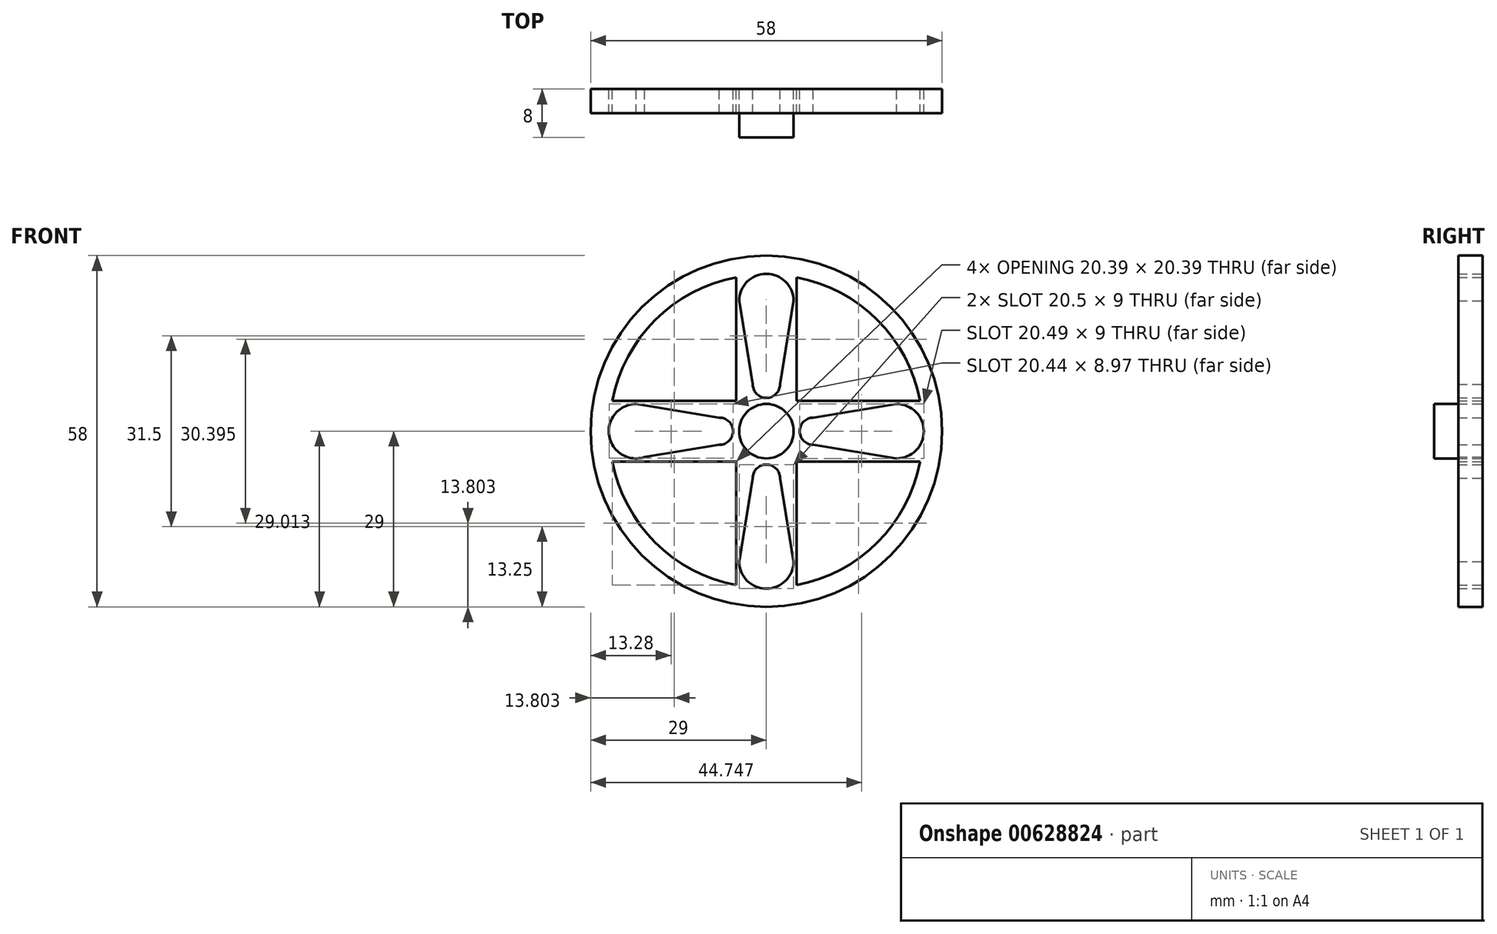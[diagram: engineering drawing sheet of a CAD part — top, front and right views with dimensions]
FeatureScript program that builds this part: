
annotation { "Feature Type Name" : "Feature", "Feature Type Description" : "" }
export const myFeature = defineFeature(function(context is Context, id is Id, definition is map)
    precondition{}
    {
        {
            var Q0;
            Q0=qCreatedBy(makeId("Front.planeOp"),FACE);
            var sketch = newSketch(context, id + "F0", { "sketchPlane" : qUnion([Q0])});
            skCircle(sketch, "E0", {"center": v(0, 0) * mm, "radius": 27 * mm});
            skCircle(sketch, "E1", {"center": v(0, 0) * mm, "radius": 4.5 * mm});
            skCircle(sketch, "E2", {"center": v(0, 0) * mm, "radius": 29 * mm});
            skArc(sketch, "E3", {"start": v(-21.5, 4.5) * mm, "mid": v(-25.94, -0.73) * mm, "end": v(-20.07, -4.27) * mm});
            skArc(sketch, "E4", {"start": v(4.5, 21.5) * mm, "mid": v(0, 26) * mm, "end": v(-4.5, 21.5) * mm});
            skArc(sketch, "E5", {"start": v(-4.5, -21.5) * mm, "mid": v(0, -26) * mm, "end": v(4.5, -21.5) * mm});
            skArc(sketch, "E6", {"start": v(-7.75, -2.25) * mm, "mid": v(-5.5, 0) * mm, "end": v(-7.75, 2.25) * mm});
            skArc(sketch, "E7", {"start": v(2.25, -7.75) * mm, "mid": v(0, -5.5) * mm, "end": v(-2.25, -7.75) * mm});
            skArc(sketch, "E8", {"start": v(7.75, 2.25) * mm, "mid": v(5.5, 0) * mm, "end": v(7.75, -2.25) * mm});
            skArc(sketch, "E9", {"start": v(-2.25, 7.75) * mm, "mid": v(0, 5.5) * mm, "end": v(2.25, 7.75) * mm});
            skLineSegment(sketch, "E10", {"start": v(-21.5, 4.5) * mm, "end": v(-7.75, 2.25) * mm});
            skLineSegment(sketch, "E11", {"start": v(-20.07, -4.27) * mm, "end": v(-7.75, -2.25) * mm});
            skLineSegment(sketch, "E12", {"start": v(-2.25, -7.75) * mm, "end": v(-4.5, -21.5) * mm});
            skLineSegment(sketch, "E13", {"start": v(2.25, -7.75) * mm, "end": v(4.5, -21.5) * mm});
            skLineSegment(sketch, "E14", {"start": v(2.25, 7.75) * mm, "end": v(4.5, 21.5) * mm});
            skLineSegment(sketch, "E15", {"start": v(-4.5, 21.5) * mm, "end": v(-2.25, 7.75) * mm});
            skLineSegment(sketch, "E16", {"start": v(5, -5) * mm, "end": v(5, -25.4) * mm});
            skLineSegment(sketch, "E17", {"start": v(5, -25.4) * mm, "end": v(5, -5) * mm});
            skLineSegment(sketch, "E18", {"start": v(25.4, -5) * mm, "end": v(5, -5) * mm});
            skLineSegment(sketch, "E19", {"start": v(-5, -5) * mm, "end": v(-5, -25.4) * mm});
            skLineSegment(sketch, "E20", {"start": v(-5, -25.4) * mm, "end": v(-5, -5) * mm});
            skLineSegment(sketch, "E21", {"start": v(-5, -5) * mm, "end": v(-25.4, -5) * mm});
            skLineSegment(sketch, "E22", {"start": v(5, 5) * mm, "end": v(5, 25.4) * mm});
            skLineSegment(sketch, "E23", {"start": v(-5, 5) * mm, "end": v(-25.4, 5) * mm});
            skLineSegment(sketch, "E24", {"start": v(-5, 25.4) * mm, "end": v(-5, 5) * mm});
            skPoint(sketch, "E25.orphan", {"position": v(-10.75, 10.75) * mm});
            skPoint(sketch, "E26.orphan", {"position": v(10.75, -10.5) * mm});
            skPoint(sketch, "E27.orphan", {"position": v(-10.75, -10.75) * mm});
            skPoint(sketch, "E28.orphan", {"position": v(10.75, 11) * mm});
            skLineSegment(sketch, "E29", {"start": v(5, 5) * mm, "end": v(25.4, 5) * mm});
            skArc(sketch, "E30", {"start": v(21.5, -4.5) * mm, "mid": v(26, 0) * mm, "end": v(21.5, 4.5) * mm});
            skPoint(sketch, "E31.center.orphan", {"position": v(21.5, 0.5) * mm});
            skLineSegment(sketch, "E32", {"start": v(7.75, -2.25) * mm, "end": v(21.5, -4.5) * mm});
            skLineSegment(sketch, "E33", {"start": v(7.75, 2.25) * mm, "end": v(21.5, 4.5) * mm});
            skArc(sketch, "E34", {"start": v(-25.4, -5) * mm, "mid": v(-18.36, -18.36) * mm, "end": v(-5, -25.4) * mm});
            skArc(sketch, "E35", {"start": v(5, -25.4) * mm, "mid": v(18.36, -18.36) * mm, "end": v(25.4, -5) * mm});
            skArc(sketch, "E36", {"start": v(25.4, 5) * mm, "mid": v(18.36, 18.36) * mm, "end": v(5, 25.4) * mm});
            skArc(sketch, "E37", {"start": v(-5, 25.4) * mm, "mid": v(-18.36, 18.36) * mm, "end": v(-25.4, 5) * mm});
            skSolve(sketch);
        }
        {
            var Q0;
            Q0=makeQuery(id+"F0.imprint","IMPRINT",FACE,{"disambiguationData":[TD([[makeQuery(id+"F0.imprint","IMPRINT",EDGE,{"derivedFrom":sQuery(id+"F0.wireOp",EDGE,"E1")}),1.0]])]});
            extrude(context, id + "F1", {"entities" : qUnion([Q0]), "depth" : 8 * mm, "offsetDistance" : 25 * mm});
        }
        {
            var Q0;
            Q0=makeQuery(id+"F0.imprint","IMPRINT",FACE,{"disambiguationData":[TD([[makeQuery(id+"F0.imprint","IMPRINT",EDGE,{"derivedFrom":sQuery(id+"F0.wireOp",EDGE,"E0")}),1.0]])]});
            var Q1;
            Q1=makeQuery(id+"F0.imprint","IMPRINT",FACE,{"disambiguationData":[TD([[makeQuery(id+"F0.imprint","IMPRINT",EDGE,{"derivedFrom":sQuery(id+"F0.wireOp",EDGE,"E0")}),-1.0]])]});
            extrude(context, id + "F2", {"entities" : qUnion([Q0, Q1]), "operationType" : NewBodyOperationType.ADD, "depth" : 4 * mm, "offsetDistance" : 25 * mm});
        }
    });
